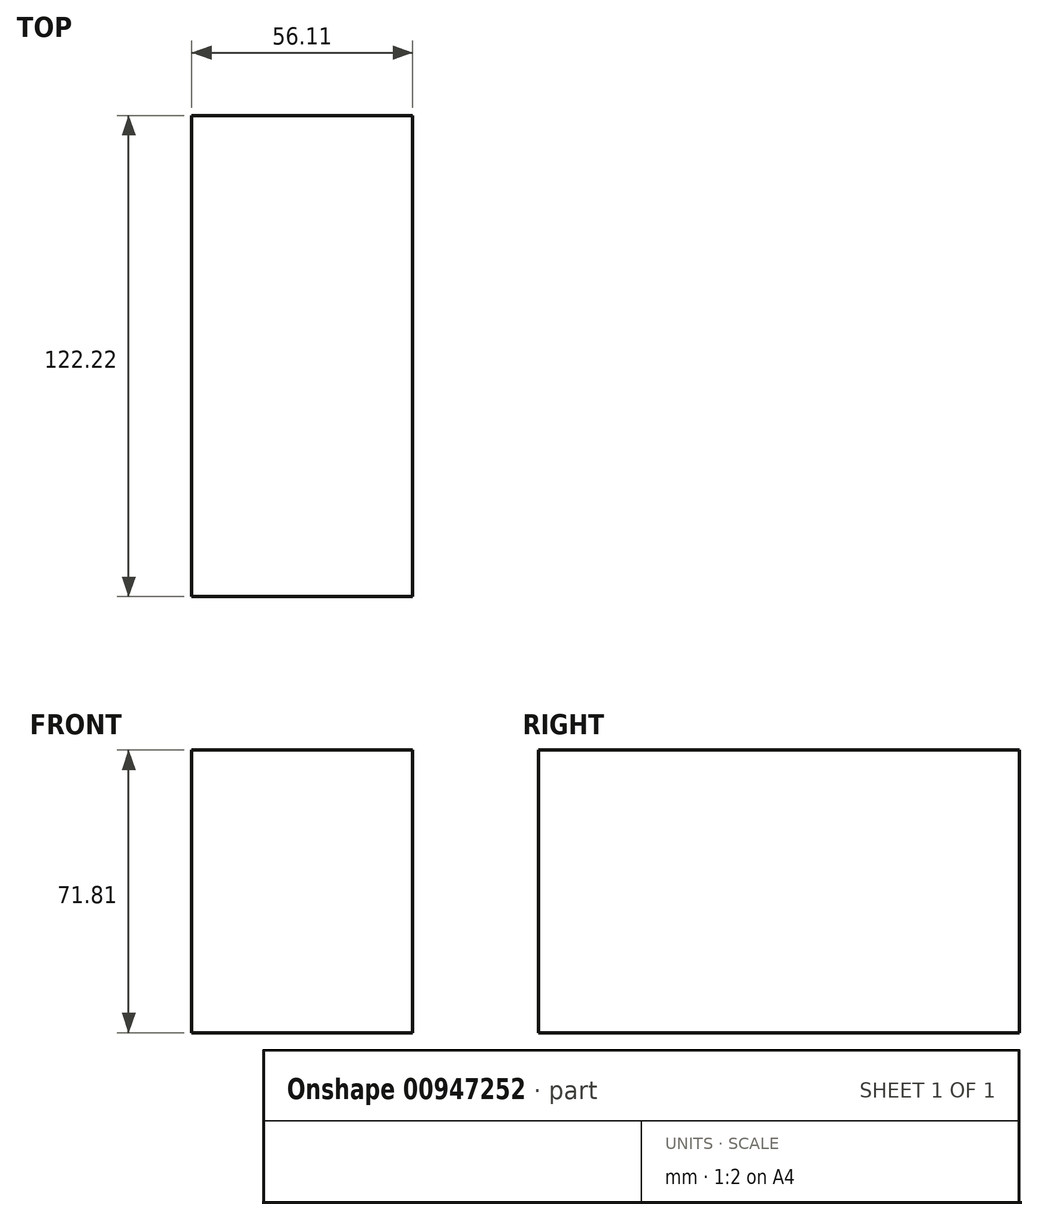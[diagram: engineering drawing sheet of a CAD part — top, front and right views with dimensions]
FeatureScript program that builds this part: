
annotation { "Feature Type Name" : "Feature", "Feature Type Description" : "" }
export const myFeature = defineFeature(function(context is Context, id is Id, definition is map)
    precondition{}
    {
        {
            var Q0;
            Q0=qCreatedBy(makeId("Front.planeOp"),FACE);
            var sketch = newSketch(context, id + "F0", { "sketchPlane" : qUnion([Q0])});
            skLineSegment(sketch, "E0.bottom", {"start": v(0, 0) * mm, "end": v(56.1, 0) * mm});
            skLineSegment(sketch, "E0.top", {"start": v(0, 71.81) * mm, "end": v(56.1, 71.81) * mm});
            skLineSegment(sketch, "E0.left", {"start": v(0, 0) * mm, "end": v(0, 71.81) * mm});
            skLineSegment(sketch, "E0.right", {"start": v(56.1, 0) * mm, "end": v(56.1, 71.81) * mm});
            skSolve(sketch);
        }
        {
            var Q0;
            Q0=makeQuery(id+"F0.imprint","IMPRINT",FACE,{"disambiguationData":[TD([[makeQuery(id+"F0.imprint","IMPRINT",EDGE,{"derivedFrom":sQuery(id+"F0.wireOp",EDGE,"E0.bottom")}),1.0]])]});
            extrude(context, id + "F1", {"entities" : qUnion([Q0]), "depth" : 122.22 * mm, "offsetDistance" : 25 * mm});
        }
    });
